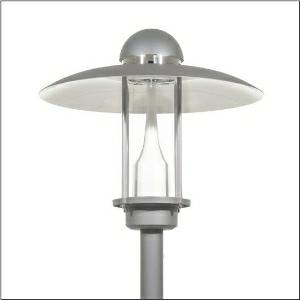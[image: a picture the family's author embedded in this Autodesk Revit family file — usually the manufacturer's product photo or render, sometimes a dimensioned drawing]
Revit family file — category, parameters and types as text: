
# Revit family: city-light_elegance_iq___st1_2a_5xa5265ef14h_e69b
name_source: partatom
category: Lighting Fixtures
units: mm (PartAtom-declared; Revit-internal decimal feet)

## family parameters
Cut with Voids When Loaded = No
Host = Face
Light Source = No
Part Type = Normal
Room Calculation Point = No
Round Connector Dimension = Use Diameter
Shared = No

## types (1)
- --- (1 x LED, 1470 lm, 10.5 W, 3000K)
    Apparent Load = 11 VA
    CIE Flux Codes = 22 62 94 98 100
    Color Rendering = 70
    Color Temperature = 3000K
    Default Elevation = 1800 mm
    Description = City-Light Elegance iQ, mast luminaire, Module 540 iQ-SR, primary light control with 3 zone facetted reflector, of plastic, silver coated, highly specular, structured, primary optical cover: cover, of PMMA, transparent, light distribution: ST1.2a, light emission: direct distribution, primary light characteristic: asymmetric, installation type: post-top, LED, High Power LED, rated luminous flux: 1.470lm, luminous efficacy: 140lm/W, light colour: 730, colour temperature: 3000K, control gear: iQ Street-Remote, control: Auto-Match, Temp-Guard, Lumen-Switch, Night-Set, Smart-Wire, Light-Fading, Desk-Remote (wireless, voltage-free reading and setting of iQ features in the workshop via application-optimized NFC function/RFID function), optimised constant luminous flux control (CLO 2.0), Street-Remote, pre-setting: logarithmic dimming characteristic, with terminal, 6-pole, max. 2.5mm², mains connection: 230..240V, AC, 50/60Hz, start of lifetime: 11W, end of service life: 11W, reduction: 5W, luminaire housing, upper part, of aluminium, coated, Siteco® metallic grey (DB 702S), diameter: 750mm, height: 675mm, spigot size: d x l = 76 x 70mm (post-top) | with reducer (optional accessory) 60 x 70mm, mounting height: 3..5m, post-top mast mounting element, of diecast aluminium, coated, Siteco® metallic grey (DB 702S), Module 540 iQ-SR, traffic white (RAL 9016), equipment: standard, protection rating (complete): IP65, insulation class (complete): insulation class II (safety insulation), certification: CE, ENEC, VDE, packaging unit: 1 piece

Light Distribution: ST1.2a
    Height = 675 mm
    Lamp = 1 x LED
    Lamp Light Flux = 1470 lm
    Lamp Power = 10.5 W
    Lamp count = 1
    Length = 750 mm
    Luminous efficacy = 140 lm/W
    Manufacturer = Siteco
    ModVariant = No
    Model = 5XA5265EF14H
    Number of Poles = 1
    OnlyDefault = Yes
    Power Factor = 1
    Product Name = City-Light Elegance iQ | ST1.2a
    Product group = mast luminaire | pylon top
    ProductGroupID = 6100
    Protection Class = Protection class II
    Protection Degree = IP 65
    RLX_Detail_Level = 1
    RLX_Emergency_Light_Flux = 0 lm
    RLX_Emergency_Type = 0
    RLX_Emergency_Type_DB = No
    RlxData = <blob elided: 60841 chars, md5=6b539e60>
    Socket = socket
    Standby Power = 0 W
    System Light Flux = 1470 lm
    System Power = 11 W
    Type Comments = factory setting: luminous flux: 100 % | dim-lin: 254 | 419 mA
    Type Image = l_1006912.jpg
    URL = http://relux.com
    VarID = @adj_159880
    Voltage = 0 V
    Weight = 0.00 kg
    Width = 0 mm  [stored 0 ft]

note: [stored X ft] marks values corroborated as IEEE doubles in the binary element streams (Revit-internal decimal feet)

## geometry (parser evidence)
native form markers: Blend x4, Sweep x11
no freeform markers — native parametric forms only
